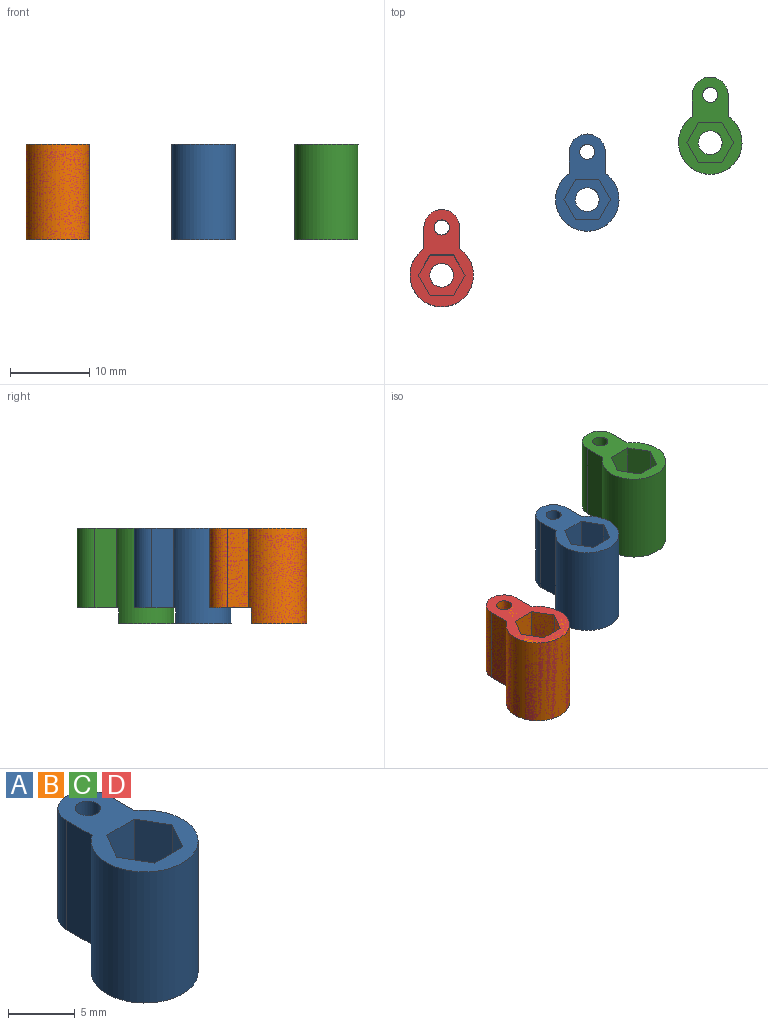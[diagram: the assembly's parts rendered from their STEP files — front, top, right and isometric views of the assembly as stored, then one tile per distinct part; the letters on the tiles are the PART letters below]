
ASSEMBLY  parts=4 mates=3
PART A: 17 faces, bbox 8x12.3x12 mm
  f0: plane 5.29x5.25mm, normal (0,0,-1), area 18.7mm2, adj f1,f2,f3,f4,f6,f7
  f1: cylinder r=2.25mm len=10mm, axis (0,0,-1), area 70.7mm2, adj f0,f2,f4,f5
  f2: plane 10x2.69mm, normal (-1,0,0), area 26.9mm2, adj f0,f1,f3,f5
  f3: cylinder r=4mm len=12mm, axis (0,0,-1), area 242.2mm2, adj f0,f2,f4,f5,f7,f8
  f4: plane 10x2.69mm, normal (1,0,0), area 26.9mm2, adj f0,f1,f3,f5
  f5: plane 12.25x8mm, normal (0,0,1), area 42.9mm2, adj f1,f2,f3,f4,f6,f9,f10,f11
  f6: cylinder r=0.95mm len=10mm, axis (0,0,-1), area 59.7mm2, adj f0,f5
  f7: plane 5.29x2mm, normal (0,1,0), area 10.6mm2, adj f0,f3,f8
  f8: plane 8x7mm, normal (0,0,-1), area 39.6mm2, adj f3,f7,f16
  f9: plane 10x2.55mm, normal (0.87,0.5,0), area 29.4mm2, adj f5,f10,f14,f15
  f10: plane 10x2.94mm, normal (0,1,0), area 29.4mm2, adj f5,f9,f11,f15
  f11: plane 10x2.55mm, normal (-0.87,0.5,0), area 29.4mm2, adj f5,f10,f12,f15
  f12: plane 10x2.55mm, normal (-0.87,-0.5,0), area 29.4mm2, adj f5,f11,f13,f15
  f13: plane 10x2.94mm, normal (0,-1,0), area 29.4mm2, adj f5,f12,f14,f15
  f14: plane 10x2.55mm, normal (0.87,-0.5,0), area 29.4mm2, adj f5,f9,f13,f15
  f15: plane 5.89x5.1mm, normal (0,0,1), area 15.5mm2, adj f9,f10,f11,f12,f13,f14,f16
  f16: cylinder r=1.5mm len=3mm, axis (0,0,-1), area 18.8mm2, adj f8,f15
PART B: same geometry as A
PART C: same geometry as A
PART D: same geometry as A
PLACE A t=(2.62,2.46,3)mm
PLACE B t=(-15.71,-7.07,3)mm
PLACE C t=(18.12,9.63,3)mm
PLACE D t=(-15.71,-7.07,3)mm
MATE planar D.f16 <-> B.f16  axis (0,0,-1) through (-15.71,-13.07,1)mm
MATE planar D.f16 <-> A.f16  axis (0,0,-1) through (-15.71,-13.07,1)mm
MATE planar C.f16 <-> D.f8  axis (0,0,-1) through (18.12,3.63,1)mm
